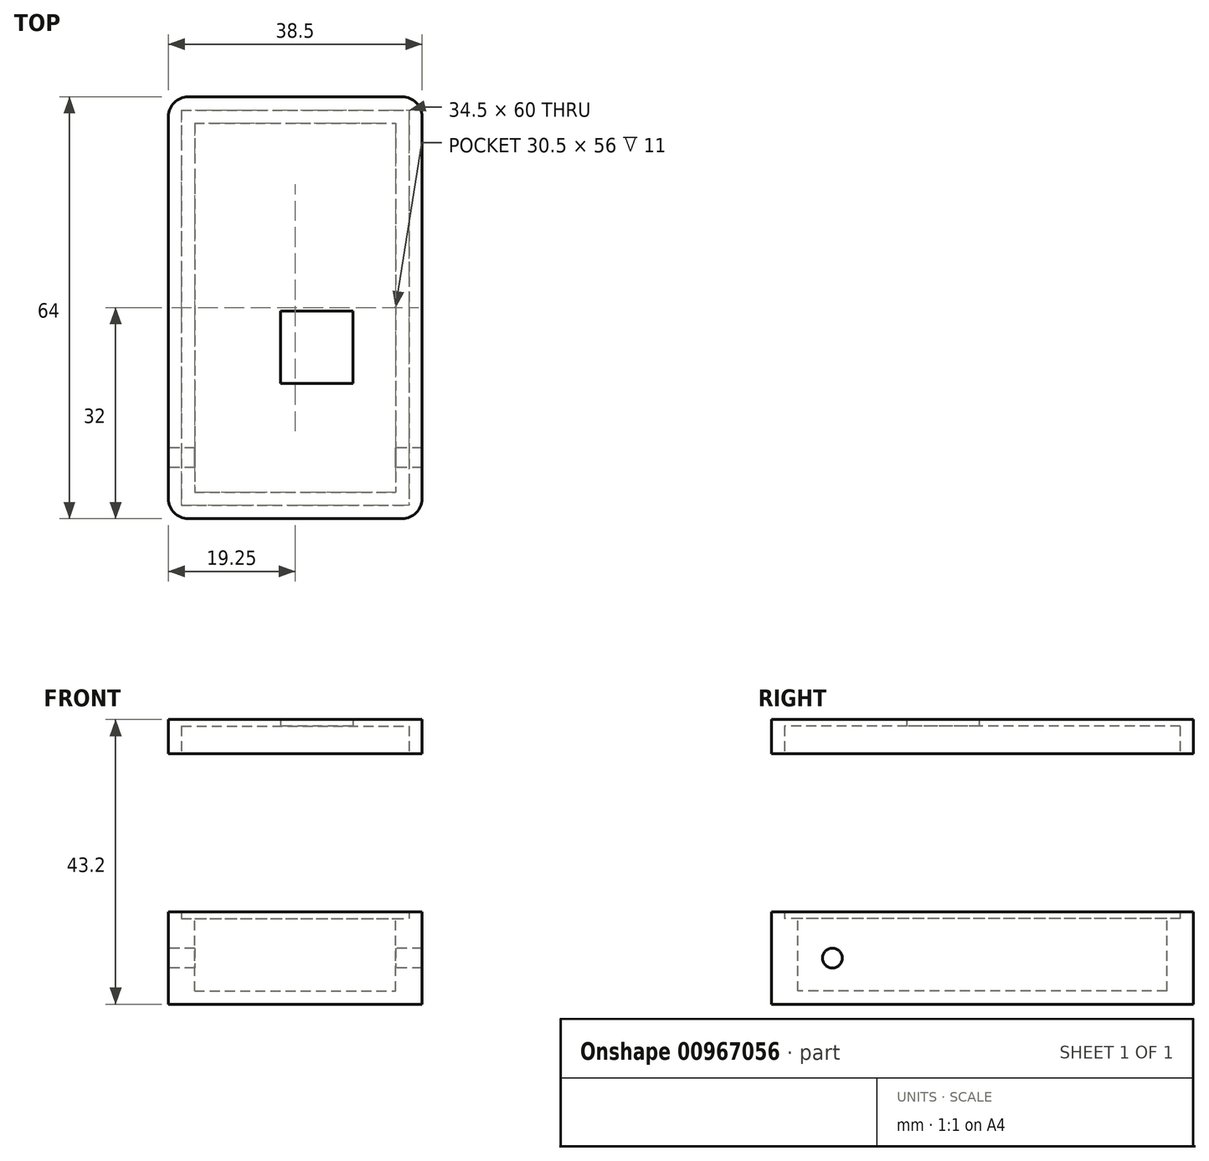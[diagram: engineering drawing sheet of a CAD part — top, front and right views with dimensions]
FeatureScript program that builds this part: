
annotation { "Feature Type Name" : "Feature", "Feature Type Description" : "" }
export const myFeature = defineFeature(function(context is Context, id is Id, definition is map)
    precondition{}
    {
        {
            var Q0;
            Q0=qCreatedBy(makeId("Top.planeOp"),FACE);
            var sketch = newSketch(context, id + "F0", { "sketchPlane" : qUnion([Q0])});
            skLineSegment(sketch, "E0.bottom", {"start": v(-16.25, 29) * mm, "end": v(16.25, 29) * mm, "construction": true});
            skLineSegment(sketch, "E0.top", {"start": v(-16.25, -29) * mm, "end": v(16.25, -29) * mm, "construction": true});
            skLineSegment(sketch, "E0.left", {"start": v(-16.25, 29) * mm, "end": v(-16.25, -29) * mm, "construction": true});
            skLineSegment(sketch, "E0.right", {"start": v(16.25, 29) * mm, "end": v(16.25, -29) * mm, "construction": true});
            skPoint(sketch, "E0.middle", {"position": v(0, 0) * mm});
            skLineSegment(sketch, "E1.0", {"start": v(-17.25, 30) * mm, "end": v(17.25, 30) * mm});
            skLineSegment(sketch, "E1.1", {"start": v(-17.25, 30) * mm, "end": v(-17.25, -30) * mm});
            skLineSegment(sketch, "E1.2", {"start": v(-17.25, -30) * mm, "end": v(17.25, -30) * mm});
            skLineSegment(sketch, "E1.3", {"start": v(17.25, 30) * mm, "end": v(17.25, -30) * mm});
            skLineSegment(sketch, "E2.0", {"start": v(-15.25, 28) * mm, "end": v(15.25, 28) * mm});
            skLineSegment(sketch, "E2.1", {"start": v(-15.25, 28) * mm, "end": v(-15.25, -28) * mm});
            skLineSegment(sketch, "E2.2", {"start": v(-15.25, -28) * mm, "end": v(15.25, -28) * mm});
            skLineSegment(sketch, "E2.3", {"start": v(15.25, 28) * mm, "end": v(15.25, -28) * mm});
            skLineSegment(sketch, "E3.0", {"start": v(-19.25, 32) * mm, "end": v(19.25, 32) * mm});
            skLineSegment(sketch, "E3.1", {"start": v(-19.25, 32) * mm, "end": v(-19.25, -32) * mm});
            skLineSegment(sketch, "E3.2", {"start": v(-19.25, -32) * mm, "end": v(19.25, -32) * mm});
            skLineSegment(sketch, "E3.3", {"start": v(19.25, 32) * mm, "end": v(19.25, -32) * mm});
            skSolve(sketch);
        }
        {
            var Q0;
            Q0 = qSketchRegion(id + "F0", true);
            var Q1;
            Q1=makeQuery(id+"F0.imprint","IMPRINT",FACE,{"disambiguationData":[TD([[makeQuery(id+"F0.imprint","IMPRINT",EDGE,{"derivedFrom":sQuery(id+"F0.wireOp",EDGE,"E1.0")}),-1.0]])]});
            var Q2;
            Q2=makeQuery(id+"F0.imprint","IMPRINT",FACE,{"disambiguationData":[TD([[makeQuery(id+"F0.imprint","IMPRINT",EDGE,{"derivedFrom":sQuery(id+"F0.wireOp",EDGE,"E2.0")}),-1.0]])]});
            extrude(context, id + "F1", {"entities" : qUnion([Q0, Q1, Q2]), "oppositeDirection" : true, "depth" : 13 * mm, "offsetDistance" : 25 * mm});
        }
        {
            var Q0;
            Q0=makeQuery(id+"F0.imprint","IMPRINT",FACE,{"disambiguationData":[TD([[makeQuery(id+"F0.imprint","IMPRINT",EDGE,{"derivedFrom":sQuery(id+"F0.wireOp",EDGE,"E1.0")}),1.0]])]});
            extrude(context, id + "F2", {"entities" : qUnion([Q0]), "operationType" : NewBodyOperationType.ADD, "depth" : 1 * mm, "offsetDistance" : 25 * mm});
        }
        {
            var Q0;
            Q0=makeQuery(id+"F0.imprint","IMPRINT",FACE,{"disambiguationData":[TD([[makeQuery(id+"F0.imprint","IMPRINT",EDGE,{"derivedFrom":sQuery(id+"F0.wireOp",EDGE,"E2.0")}),-1.0]])]});
            extrude(context, id + "F3", {"entities" : qUnion([Q0]), "operationType" : NewBodyOperationType.REMOVE, "oppositeDirection" : true, "depth" : 11 * mm, "offsetDistance" : 25 * mm});
        }
        {
            var Q0;
            {var subQ0=sQuery(id+"F0.wireOp",EDGE,"E3.2");var subQ1=sQuery(id+"F0.wireOp",EDGE,"E3.1");Q0=makeQuery(id+"F2.boolean.opBoolean","MERGE",EDGE,{"derivedFrom":[makeQuery(id+"F1.opExtrude","SWEPT_EDGE",EDGE,{"disambiguationData":[OSD([subQ1,subQ0])]}),makeQuery(id+"F2.opExtrude","SWEPT_EDGE",EDGE,{"disambiguationData":[OSD([subQ1,subQ0])]})]});}
            var Q1;
            {var subQ0=sQuery(id+"F0.wireOp",EDGE,"E3.3");var subQ1=sQuery(id+"F0.wireOp",EDGE,"E3.2");Q1=makeQuery(id+"F2.boolean.opBoolean","MERGE",EDGE,{"derivedFrom":[makeQuery(id+"F1.opExtrude","SWEPT_EDGE",EDGE,{"disambiguationData":[OSD([subQ1,subQ0])]}),makeQuery(id+"F2.opExtrude","SWEPT_EDGE",EDGE,{"disambiguationData":[OSD([subQ1,subQ0])]})]});}
            var Q2;
            {var subQ0=sQuery(id+"F0.wireOp",EDGE,"E3.3");var subQ1=sQuery(id+"F0.wireOp",EDGE,"E3.0");Q2=makeQuery(id+"F2.boolean.opBoolean","MERGE",EDGE,{"derivedFrom":[makeQuery(id+"F1.opExtrude","SWEPT_EDGE",EDGE,{"disambiguationData":[OSD([subQ1,subQ0])]}),makeQuery(id+"F2.opExtrude","SWEPT_EDGE",EDGE,{"disambiguationData":[OSD([subQ1,subQ0])]})]});}
            var Q3;
            {var subQ0=sQuery(id+"F0.wireOp",EDGE,"E3.1");var subQ1=sQuery(id+"F0.wireOp",EDGE,"E3.0");Q3=makeQuery(id+"F2.boolean.opBoolean","MERGE",EDGE,{"derivedFrom":[makeQuery(id+"F1.opExtrude","SWEPT_EDGE",EDGE,{"disambiguationData":[OSD([subQ1,subQ0])]}),makeQuery(id+"F2.opExtrude","SWEPT_EDGE",EDGE,{"disambiguationData":[OSD([subQ1,subQ0])]})]});}
            fillet(context, id + "F4", {"entities" : qUnion([Q0, Q1, Q2, Q3]), "radius" : 3 * mm, "tangentPropagation" : true, "allowEdgeOverflow" : false});
        }
        {
            var Q0;
            {var subQ0=sQuery(id+"F0.wireOp",EDGE,"E3.1");Q0=makeQuery(id+"F2.boolean.opBoolean","MERGE",FACE,{"derivedFrom":[makeQuery(id+"F1.opExtrude","SWEPT_FACE",FACE,{"disambiguationData":[OSD([subQ0])]}),makeQuery(id+"F2.opExtrude","SWEPT_FACE",FACE,{"disambiguationData":[OSD([subQ0])]})]});}
            var sketch = newSketch(context, id + "F5", { "sketchPlane" : qUnion([Q0])});
            skLineSegment(sketch, "E4.0", {"start": v(-29, 1) * mm, "end": v(29, 1) * mm, "construction": true});
            skLineSegment(sketch, "E4.1", {"start": v(-29, 1) * mm, "end": v(-29, -13) * mm, "construction": true});
            skLineSegment(sketch, "E4.2", {"start": v(-29, -13) * mm, "end": v(29, -13) * mm, "construction": true});
            skLineSegment(sketch, "E4.3", {"start": v(29, -13) * mm, "end": v(29, 1) * mm, "construction": true});
            skLineSegment(sketch, "E5", {"start": v(29, -6) * mm, "end": v(-29, -6) * mm, "construction": true});
            skPoint(sketch, "E6", {"position": v(22.75, -6) * mm});
            skCircle(sketch, "E7", {"center": v(22.75, -6) * mm, "radius": 1.5 * mm});
            skSolve(sketch);
        }
        {
            var Q0;
            Q0 = qSketchRegion(id + "F5", true);
            extrude(context, id + "F6", {"entities" : qUnion([Q0]), "operationType" : NewBodyOperationType.REMOVE, "endBound" : BoundingType.THROUGH_ALL, "oppositeDirection" : true, "depth" : 25 * mm, "offsetDistance" : 25 * mm});
        }
        {
            var Q0;
            Q0=qCreatedBy(makeId("Top.planeOp"),FACE);
            cPlane(context, id + "F7", {"entities" : qUnion([Q0]), "cplaneType" : CPlaneType.OFFSET, "offset" : 25 * mm, "width" : 150 * mm, "height" : 150 * mm});
        }
        {
            var Q0;
            Q0=qCreatedBy(id+"F7.planeOp",FACE);
            var sketch = newSketch(context, id + "F8", { "sketchPlane" : qUnion([Q0])});
            skLineSegment(sketch, "E8.0", {"start": v(-15.25, 28) * mm, "end": v(-15.25, -28) * mm});
            skLineSegment(sketch, "E8.1", {"start": v(-15.25, 28) * mm, "end": v(15.25, 28) * mm});
            skLineSegment(sketch, "E8.2", {"start": v(15.25, 28) * mm, "end": v(15.25, -28) * mm});
            skLineSegment(sketch, "E8.3", {"start": v(-15.25, -28) * mm, "end": v(15.25, -28) * mm});
            skLineSegment(sketch, "E8.4", {"start": v(-17.25, 30) * mm, "end": v(-17.25, -30) * mm});
            skLineSegment(sketch, "E8.5", {"start": v(-17.25, -30) * mm, "end": v(17.25, -30) * mm});
            skLineSegment(sketch, "E8.6", {"start": v(17.25, 30) * mm, "end": v(17.25, -30) * mm});
            skLineSegment(sketch, "E8.7", {"start": v(-17.25, 30) * mm, "end": v(17.25, 30) * mm});
            skLineSegment(sketch, "E8.8", {"start": v(-19.25, 32) * mm, "end": v(19.25, 32) * mm});
            skLineSegment(sketch, "E8.9", {"start": v(-19.25, 32) * mm, "end": v(-19.25, -32) * mm});
            skLineSegment(sketch, "E8.10", {"start": v(-19.25, -32) * mm, "end": v(19.25, -32) * mm});
            skLineSegment(sketch, "E8.11", {"start": v(19.25, 32) * mm, "end": v(19.25, -32) * mm});
            skLineSegment(sketch, "E9.0", {"start": v(-16.25, 29) * mm, "end": v(-16.25, -29) * mm, "construction": true});
            skLineSegment(sketch, "E9.1", {"start": v(-16.25, -29) * mm, "end": v(16.25, -29) * mm, "construction": true});
            skLineSegment(sketch, "E9.2", {"start": v(16.25, 29) * mm, "end": v(16.25, -29) * mm, "construction": true});
            skLineSegment(sketch, "E9.3", {"start": v(-16.25, 29) * mm, "end": v(16.25, 29) * mm, "construction": true});
            skPoint(sketch, "E10", {"position": v(8.75, -0.5) * mm});
            skLineSegment(sketch, "E11.bottom", {"start": v(8.75, -0.5) * mm, "end": v(-2.25, -0.5) * mm});
            skLineSegment(sketch, "E11.top", {"start": v(8.75, -11.5) * mm, "end": v(-2.25, -11.5) * mm});
            skLineSegment(sketch, "E11.left", {"start": v(8.75, -0.5) * mm, "end": v(8.75, -11.5) * mm});
            skLineSegment(sketch, "E11.right", {"start": v(-2.25, -0.5) * mm, "end": v(-2.25, -11.5) * mm});
            skSolve(sketch);
        }
        {
            var Q0;
            Q0=makeQuery(id+"F8.imprint","IMPRINT",FACE,{"disambiguationData":[TD([[makeQuery(id+"F8.imprint","IMPRINT",EDGE,{"derivedFrom":sQuery(id+"F8.wireOp",EDGE,"E8.4")}),-1.0]])]});
            var Q1;
            Q1=makeQuery(id+"F8.imprint","IMPRINT",FACE,{"disambiguationData":[TD([[makeQuery(id+"F8.imprint","IMPRINT",EDGE,{"derivedFrom":sQuery(id+"F8.wireOp",EDGE,"E8.0")}),1.0]])]});
            var Q2;
            Q2=makeQuery(id+"F8.imprint","IMPRINT",FACE,{"disambiguationData":[TD([[makeQuery(id+"F8.imprint","IMPRINT",EDGE,{"derivedFrom":sQuery(id+"F8.wireOp",EDGE,"E8.0")}),-1.0]])]});
            extrude(context, id + "F9", {"entities" : qUnion([Q0, Q1, Q2]), "depth" : (1.2 - 1 + 5) * mm, "offsetDistance" : 25 * mm});
        }
        {
            var Q0;
            Q0=makeQuery(id+"F8.imprint","IMPRINT",FACE,{"disambiguationData":[TD([[makeQuery(id+"F8.imprint","IMPRINT",EDGE,{"derivedFrom":sQuery(id+"F8.wireOp",EDGE,"E8.0")}),-1.0]])]});
            var Q1;
            Q1=makeQuery(id+"F8.imprint","IMPRINT",FACE,{"disambiguationData":[TD([[makeQuery(id+"F8.imprint","IMPRINT",EDGE,{"derivedFrom":sQuery(id+"F8.wireOp",EDGE,"E8.0")}),1.0]])]});
            extrude(context, id + "F10", {"entities" : qUnion([Q0, Q1]), "operationType" : NewBodyOperationType.REMOVE, "depth" : (1.2 - 1 + 5 - 1) * mm, "offsetDistance" : 25 * mm});
        }
        {
            var Q0;
            Q0=makeQuery(id+"F9.opExtrude","SWEPT_EDGE",EDGE,{"disambiguationData":[OSD([sQuery(id+"F8.wireOp",EDGE,"E8.9"),sQuery(id+"F8.wireOp",EDGE,"E8.10")])]});
            var Q1;
            Q1=makeQuery(id+"F9.opExtrude","SWEPT_EDGE",EDGE,{"disambiguationData":[OSD([sQuery(id+"F8.wireOp",EDGE,"E8.10"),sQuery(id+"F8.wireOp",EDGE,"E8.11")])]});
            var Q2;
            Q2=makeQuery(id+"F9.opExtrude","SWEPT_EDGE",EDGE,{"disambiguationData":[OSD([sQuery(id+"F8.wireOp",EDGE,"E8.8"),sQuery(id+"F8.wireOp",EDGE,"E8.11")])]});
            var Q3;
            Q3=makeQuery(id+"F9.opExtrude","SWEPT_EDGE",EDGE,{"disambiguationData":[OSD([sQuery(id+"F8.wireOp",EDGE,"E8.8"),sQuery(id+"F8.wireOp",EDGE,"E8.9")])]});
            fillet(context, id + "F11", {"entities" : qUnion([Q0, Q1, Q2, Q3]), "radius" : 3 * mm, "tangentPropagation" : true, "allowEdgeOverflow" : false});
        }
    });
